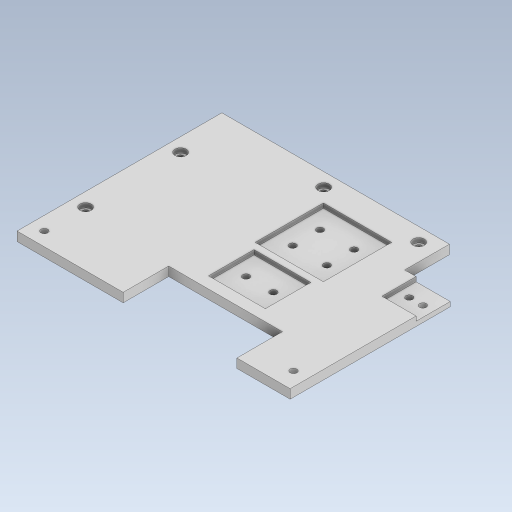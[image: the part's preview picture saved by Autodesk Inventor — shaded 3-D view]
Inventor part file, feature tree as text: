
AUTODESK INVENTOR PART (.ipt)
format: ipt  version: 2023.5 (Build 275446000, 446)  size: 170,496 bytes
history: native  units: in
note: dims shown in document units (in); Inventor stores cm internally (conversion verified against a paired STEP export)
features: extrude x2, sketch x1
ambient origin geometry x8: Origin, YZ Plane, XZ Plane, XY Plane, X Axis, Y Axis, Z Axis, Center Point
bodies: Solid1 (feature_tree)
feature tree (3):
  sketch  "Sketch1"  dims[d28=0.1575in d29=0.0in d30=0.0787in d31=0.0in d32=0.2953in d33=0.4724in d34=0.4724in d35=0.2953in d36=0.0in d37=0.0in d38=0.1969in]
  extrude  "Extrusion1"  Depth=0.0787in TaperAngle=0.0deg
  extrude  "Extrusion2"  Depth=0.1969in
